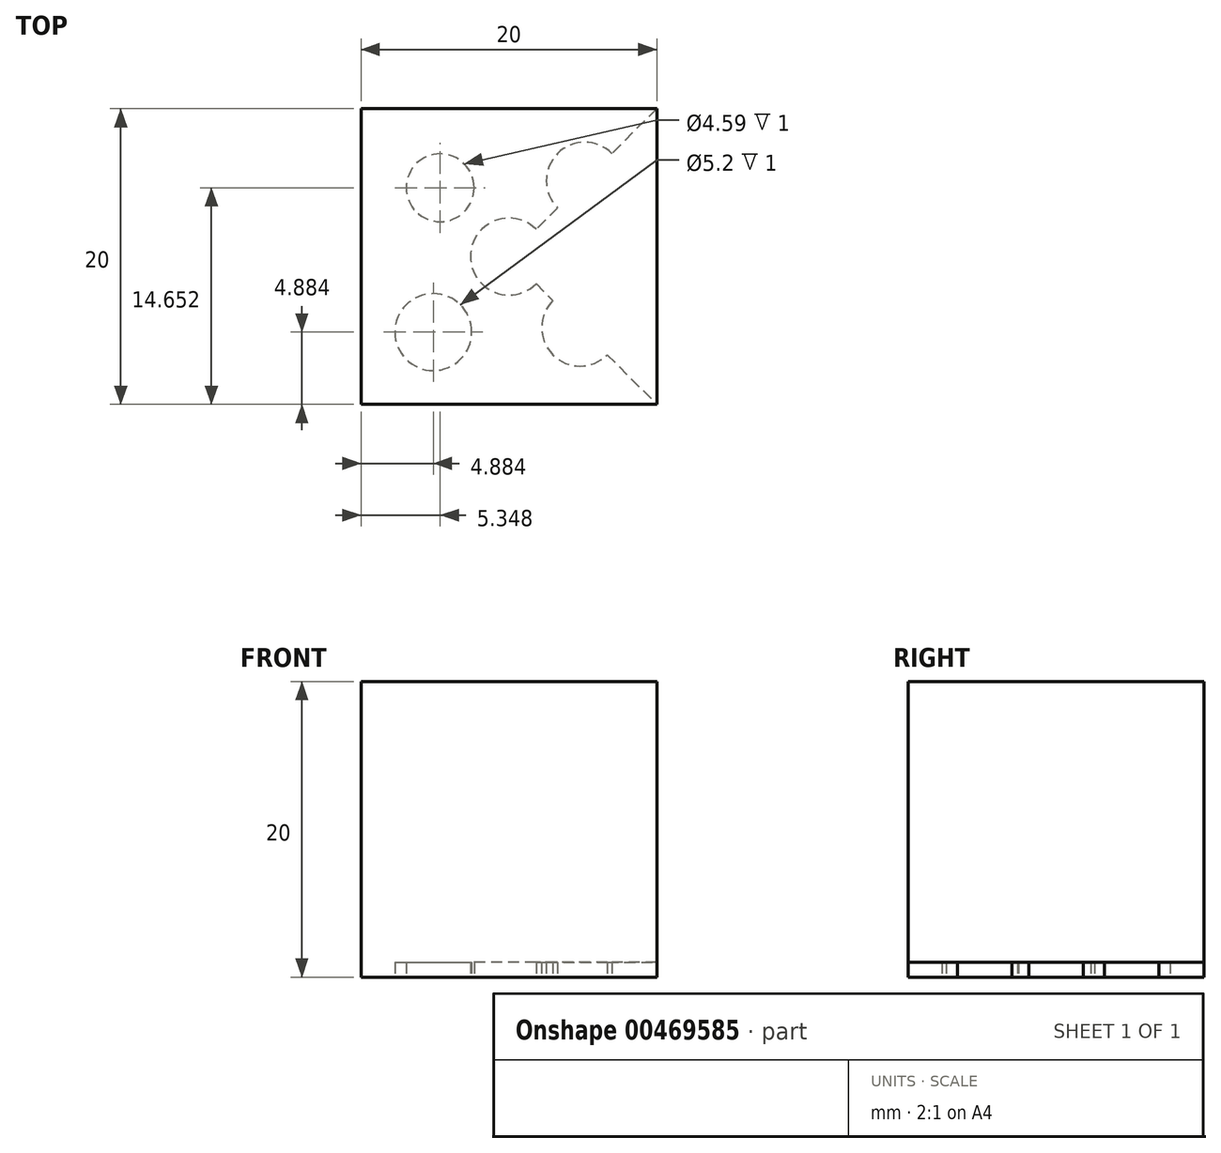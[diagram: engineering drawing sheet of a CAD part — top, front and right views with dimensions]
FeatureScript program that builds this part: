
annotation { "Feature Type Name" : "Feature", "Feature Type Description" : "" }
export const myFeature = defineFeature(function(context is Context, id is Id, definition is map)
    precondition{}
    {
        {
            var Q0;
            Q0=qCreatedBy(makeId("Front.planeOp"),FACE);
            var sketch = newSketch(context, id + "F0", { "sketchPlane" : qUnion([Q0])});
            skLineSegment(sketch, "E0.bottom", {"start": v(0, 0) * mm, "end": v(-20, 0) * mm});
            skLineSegment(sketch, "E0.top", {"start": v(0, -20) * mm, "end": v(-20, -20) * mm});
            skLineSegment(sketch, "E0.left", {"start": v(0, 0) * mm, "end": v(0, -20) * mm});
            skLineSegment(sketch, "E0.right", {"start": v(-20, 0) * mm, "end": v(-20, -20) * mm});
            skSolve(sketch);
        }
        {
            var Q0;
            Q0 = qSketchRegion(id + "F0", true);
            extrude(context, id + "F1", {"entities" : qUnion([Q0]), "depth" : 20 * mm});
        }
        {
            var Q0;
            Q0=makeQuery(id+"F1.opExtrude","SWEPT_FACE",FACE,{"disambiguationData":[OSD([sQuery(id+"F0.wireOp",EDGE,"E0.top")])]});
            var sketch = newSketch(context, id + "F2", { "sketchPlane" : qUnion([Q0])});
            skLineSegment(sketch, "E1", {"start": v(-20, 0) * mm, "end": v(0, 20) * mm});
            skLineSegment(sketch, "E2", {"start": v(0, 20) * mm, "end": v(0, 0) * mm});
            skLineSegment(sketch, "E3", {"start": v(0, 0) * mm, "end": v(-20, 20) * mm});
            skCircle(sketch, "E4", {"center": v(-10, 10) * mm, "radius": 2.6 * mm});
            skCircle(sketch, "E5", {"center": v(-4.87, 4.87) * mm, "radius": 2.6 * mm});
            skCircle(sketch, "E6", {"center": v(-14.65, 5.35) * mm, "radius": 2.3 * mm});
            skCircle(sketch, "E7", {"center": v(-5.19, 14.81) * mm, "radius": 2.6 * mm});
            skCircle(sketch, "E8", {"center": v(-15.12, 15.12) * mm, "radius": 2.6 * mm});
            skSolve(sketch);
        }
        {
            var Q0;
            Q0 = qSketchRegion(id + "F2", true);
            extrude(context, id + "F3", {"entities" : qUnion([Q0]), "operationType" : NewBodyOperationType.REMOVE, "oppositeDirection" : true, "depth" : 1 * mm});
        }
    });
